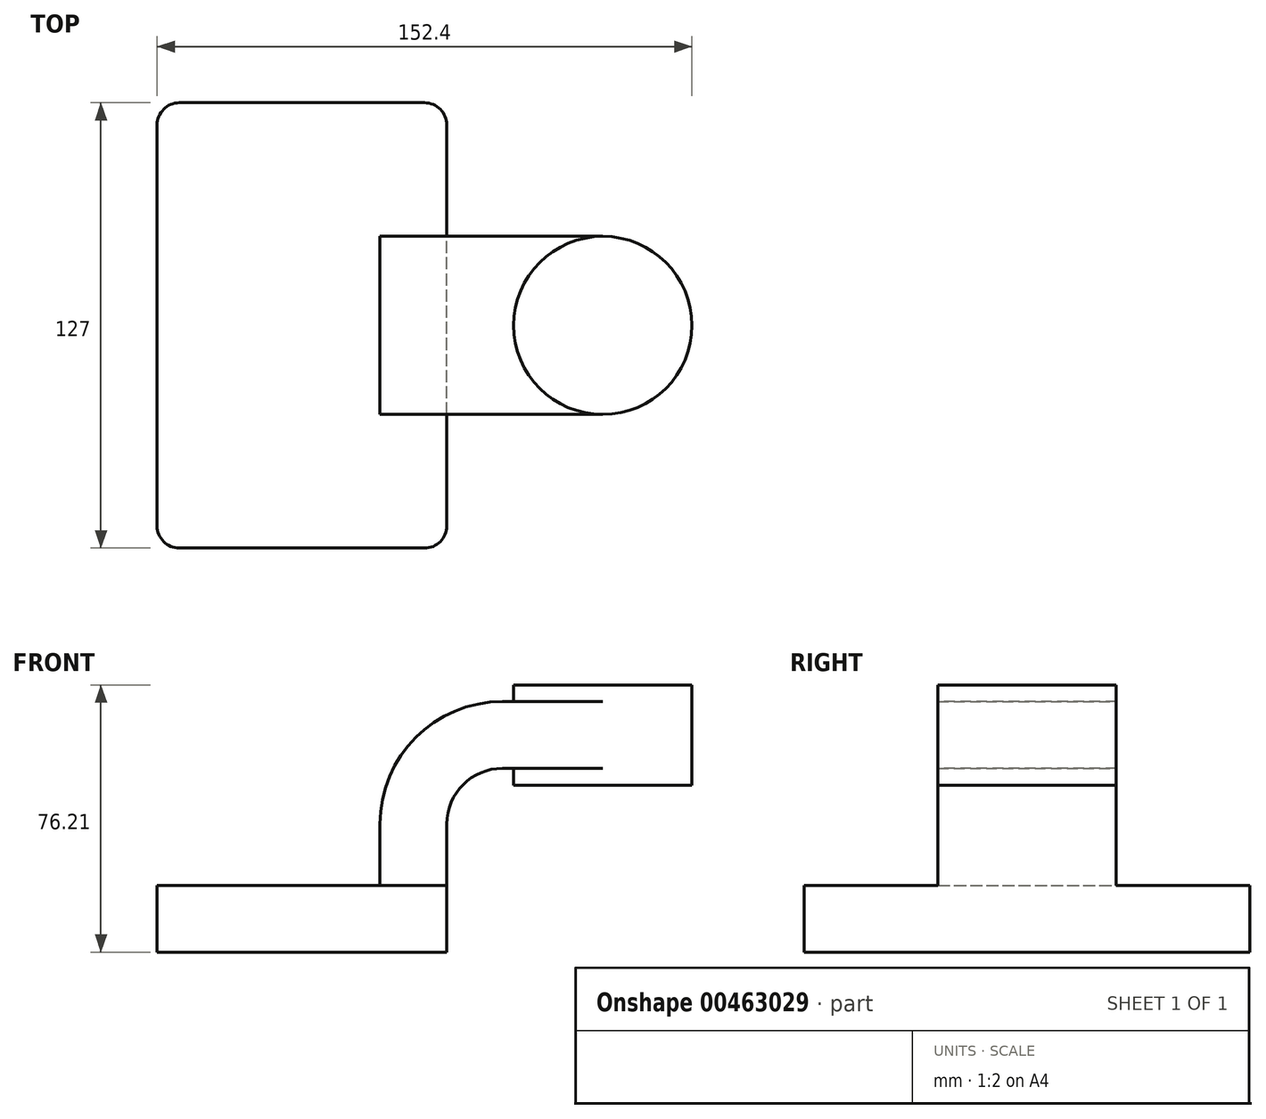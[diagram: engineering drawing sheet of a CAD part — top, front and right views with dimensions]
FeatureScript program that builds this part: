
annotation { "Feature Type Name" : "Feature", "Feature Type Description" : "" }
export const myFeature = defineFeature(function(context is Context, id is Id, definition is map)
    precondition{}
    {
        {
            var Q0;
            Q0=qCreatedBy(makeId("Front.planeOp"),FACE);
            var sketch = newSketch(context, id + "F0", { "sketchPlane" : qUnion([Q0])});
            skLineSegment(sketch, "E0.bottom", {"start": v(41.28, -9.52) * mm, "end": v(-41.27, -9.53) * mm});
            skLineSegment(sketch, "E0.top", {"start": v(41.27, 9.53) * mm, "end": v(-41.28, 9.53) * mm});
            skLineSegment(sketch, "E0.left", {"start": v(41.28, -9.52) * mm, "end": v(41.28, 9.53) * mm});
            skLineSegment(sketch, "E0.right", {"start": v(-41.27, -9.53) * mm, "end": v(-41.28, 9.53) * mm});
            skPoint(sketch, "E0.middle", {"position": v(0, 0) * mm});
            skLineSegment(sketch, "E1.bottom", {"start": v(111.13, 38.1) * mm, "end": v(60.33, 38.1) * mm});
            skLineSegment(sketch, "E1.top", {"start": v(111.13, 66.68) * mm, "end": v(60.33, 66.68) * mm});
            skLineSegment(sketch, "E1.left", {"start": v(111.13, 38.1) * mm, "end": v(111.13, 66.68) * mm});
            skLineSegment(sketch, "E1.right", {"start": v(60.33, 38.1) * mm, "end": v(60.33, 66.67) * mm});
            skPoint(sketch, "E1.middle", {"position": v(85.73, 52.39) * mm});
            skLineSegment(sketch, "E2", {"start": v(41.27, 9.53) * mm, "end": v(41.27, 27) * mm});
            skArc(sketch, "E3", {"start": v(41.27, 27) * mm, "mid": v(45.92, 38.23) * mm, "end": v(57.15, 42.88) * mm});
            skLineSegment(sketch, "E4", {"start": v(57.15, 42.88) * mm, "end": v(85.73, 42.88) * mm});
            skLineSegment(sketch, "E5.0", {"start": v(57.15, 61.93) * mm, "end": v(85.73, 61.93) * mm});
            skArc(sketch, "E5.1", {"start": v(22.23, 27) * mm, "mid": v(32.45, 51.7) * mm, "end": v(57.15, 61.93) * mm});
            skLineSegment(sketch, "E5.2", {"start": v(22.22, 9.53) * mm, "end": v(22.22, 27) * mm});
            skFitSpline(sketch, "E6", {"points": [v(-41.28, 9.52) * mm, v(57.15, 61.93) * mm], "startDerivative": vector(23.48, 101.63) * mm, "endDerivative": vector(143.46, -11.83) * mm});
            skLineSegment(sketch, "E7", {"start": v(85.73, 66.68) * mm, "end": v(85.73, 38.1) * mm});
            skSolve(sketch);
        }
        {
            var Q0;
            Q0=makeQuery(id+"F0.imprint","IMPRINT",FACE,{"disambiguationData":[TD([[makeQuery(id+"F0.imprint","IMPRINT",EDGE,{"derivedFrom":sQuery(id+"F0.wireOp",EDGE,"E0.bottom")}),-1.0]])]});
            extrude(context, id + "F1", {"entities" : qUnion([Q0]), "endBound" : BoundingType.SYMMETRIC, "depth" : 127 * mm});
        }
        {
            var Q0;
            {var subQ0=sQuery(id+"F0.wireOp",EDGE,"E4");var subQ1=sQuery(id+"F0.wireOp",EDGE,"E1.right");var subQ2=makeQuery(id+"F0.imprint","INTERSECT",VERTEX,{"derivedFrom":[subQ1,subQ0]});Q0=makeQuery(id+"F0.imprint","IMPRINT",FACE,{"disambiguationData":[TD([[makeQuery(id+"F0.imprint","IMPRINT",EDGE,{"disambiguationData":[TD([[subQ2,-1.0]])],"derivedFrom":subQ1}),-1.0]])]});}
            var Q1;
            {var subQ1=sQuery(id+"F0.wireOp",EDGE,"E2");Q1=makeQuery(id+"F0.imprint","IMPRINT",FACE,{"disambiguationData":[TD([[makeQuery(id+"F0.imprint","IMPRINT",EDGE,{"derivedFrom":subQ1}),1.0]])]});}
            extrude(context, id + "F2", {"entities" : qUnion([Q0, Q1]), "operationType" : NewBodyOperationType.ADD, "endBound" : BoundingType.SYMMETRIC, "depth" : 50.8 * mm});
        }
        {
            var Q0;
            Q0=makeQuery(id+"F0.imprint","IMPRINT",FACE,{"disambiguationData":[TD([[makeQuery(id+"F0.imprint","IMPRINT",EDGE,{"derivedFrom":sQuery(id+"F0.wireOp",EDGE,"E5.1")}),1.0]])]});
            extrude(context, id + "F3", {"entities" : qUnion([Q0]), "operationType" : NewBodyOperationType.ADD, "endBound" : BoundingType.SYMMETRIC, "depth" : 15.88 * mm});
        }
        {
            var Q0;
            {var subQ0=sQuery(id+"F0.wireOp",EDGE,"E1.left");Q0=makeQuery(id+"F0.imprint","IMPRINT",FACE,{"disambiguationData":[TD([[makeQuery(id+"F0.imprint","IMPRINT",EDGE,{"derivedFrom":subQ0}),1.0]])]});}
            var Q1;
            Q1=sQuery(id+"F0.wireOp",EDGE,"E7");
            revolve(context, id + "F4", {"operationType" : NewBodyOperationType.ADD, "entities" : qUnion([Q0]), "axis" : qUnion([Q1]), "revolveType" : RevolveType.FULL});
        }
        {
            var Q0;
            Q0=makeQuery(id+"F1.opExtrude","CAP_EDGE",EDGE,{"disambiguationData":[OSD([sQuery(id+"F0.wireOp",EDGE,"E0.right")])],"isStart":false});
            var Q1;
            Q1=makeQuery(id+"F1.opExtrude","CAP_EDGE",EDGE,{"disambiguationData":[OSD([sQuery(id+"F0.wireOp",EDGE,"E0.left")])],"isStart":false});
            var Q2;
            Q2=makeQuery(id+"F1.opExtrude","CAP_EDGE",EDGE,{"disambiguationData":[OSD([sQuery(id+"F0.wireOp",EDGE,"E0.left")])],"isStart":true});
            var Q3;
            Q3=makeQuery(id+"F1.opExtrude","CAP_EDGE",EDGE,{"disambiguationData":[OSD([sQuery(id+"F0.wireOp",EDGE,"E0.right")])],"isStart":true});
            fillet(context, id + "F5", {"entities" : qUnion([Q0, Q1, Q2, Q3]), "radius" : 6.35 * mm, "tangentPropagation" : true, "allowEdgeOverflow" : false});
        }
    });
